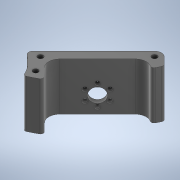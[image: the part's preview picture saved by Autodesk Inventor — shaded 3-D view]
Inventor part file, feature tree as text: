
AUTODESK INVENTOR PART (.ipt)
format: ipt  version: 2020 (Build 240168000, 168)  size: 754,176 bytes
history: native  units: mm
features: sketch x7, extrude x7, chamfer x2, projected_geometry x2, other x1, fillet x1
ambient origin geometry x8: Origin, YZ Plane, XZ Plane, XY Plane, X Axis, Y Axis, Z Axis, Center Point
bodies: Body1 (feature_tree)
feature tree (20):
  other  "Твердое тело1"
  sketch  "Эскиз1"
  extrude  "Выдавливание10"  Depth=3.8mm
  sketch  "Эскиз6"
  extrude  "Выдавливание13"  Depth=6.0mm
  extrude  "Выдавливание14"  Depth=35.0mm TaperAngle=0.0deg
  chamfer  "Фаска3"  Distance=59.0mm
  extrude  "Выдавливание15"  Depth=21.3mm
  fillet  "Сопряжение1"  Radius=15.0mm
  extrude  "Выдавливание16"  Depth=10.4mm
  extrude  "Выдавливание17"  Depth=2.5mm
  sketch  "Эскиз10"
  extrude  "Выдавливание18"  Depth=60.0mm TaperAngle=360.0deg
  chamfer  "Фаска4"  Distance=33.5mm
  sketch  "Эскиз7"
  sketch  "Эскиз8"
  projected_geometry  "Спроецированная петля3"
  sketch  "Эскиз9"
  projected_geometry  "Спроецированная петля4"
  sketch  "Эскиз11"
